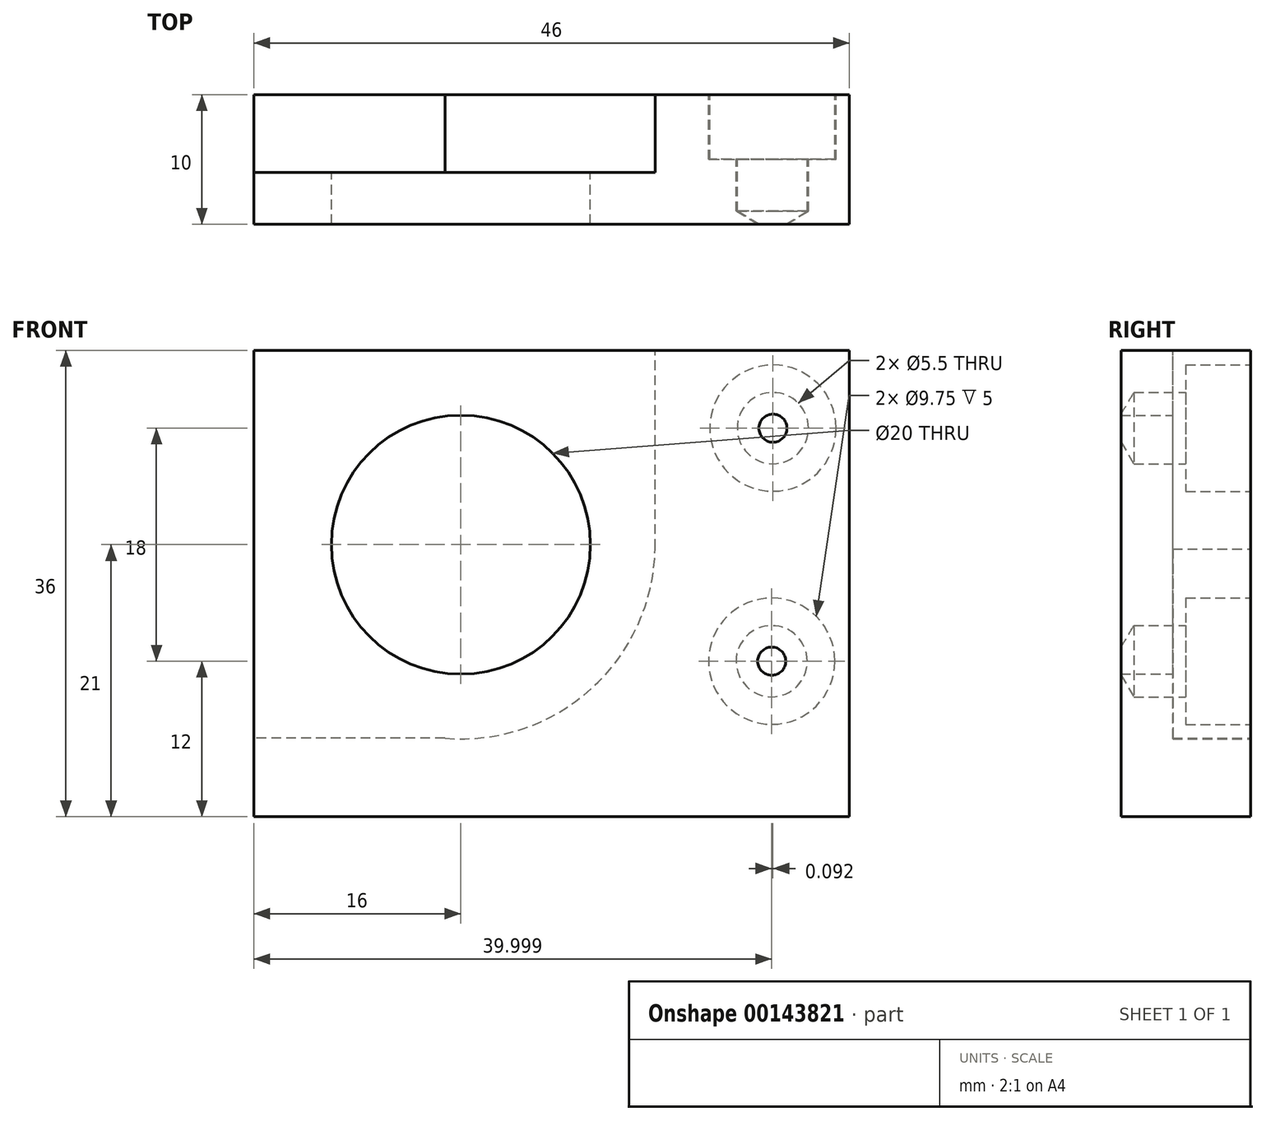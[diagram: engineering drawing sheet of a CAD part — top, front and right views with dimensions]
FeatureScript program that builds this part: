
annotation { "Feature Type Name" : "Feature", "Feature Type Description" : "" }
export const myFeature = defineFeature(function(context is Context, id is Id, definition is map)
    precondition{}
    {
        {
            var Q0;
            Q0=qCreatedBy(makeId("Front.planeOp"),FACE);
            var sketch = newSketch(context, id + "F0", { "sketchPlane" : qUnion([Q0])});
            skLineSegment(sketch, "E0.bottom", {"start": v(23, -18) * mm, "end": v(-23, -18) * mm});
            skLineSegment(sketch, "E0.top", {"start": v(23, 18) * mm, "end": v(-23, 18) * mm});
            skLineSegment(sketch, "E0.left", {"start": v(23, -18) * mm, "end": v(23, 18) * mm});
            skLineSegment(sketch, "E0.right", {"start": v(-23, -18) * mm, "end": v(-23, 18) * mm});
            skPoint(sketch, "E0.middle", {"position": v(0, 0) * mm});
            skCircle(sketch, "E1", {"center": v(-7, 3) * mm, "radius": 10 * mm});
            skSolve(sketch);
        }
        {
            var Q0;
            Q0=makeQuery(id+"F0.imprint","IMPRINT",FACE,{"disambiguationData":[TD([[makeQuery(id+"F0.imprint","IMPRINT",EDGE,{"derivedFrom":sQuery(id+"F0.wireOp",EDGE,"E0.bottom")}),-1.0]])]});
            extrude(context, id + "F1", {"entities" : qUnion([Q0]), "depth" : 10 * mm});
        }
        {
            var Q0;
            Q0=makeQuery(id+"F1.opExtrude","CAP_FACE",FACE,{"disambiguationData":[OSD([sQuery(id+"F0.wireOp",EDGE,"E0.bottom"),sQuery(id+"F0.wireOp",EDGE,"E0.top"),sQuery(id+"F0.wireOp",EDGE,"E0.left"),sQuery(id+"F0.wireOp",EDGE,"E0.right"),sQuery(id+"F0.wireOp",EDGE,"aKu84cq8-YSLd-acEW-WYgU-Aiw9NU1RKzbg")])],"isStart":true});
            var sketch = newSketch(context, id + "F2", { "sketchPlane" : qUnion([Q0])});
            skCircle(sketch, "E2", {"center": v(-17.1, 12) * mm, "radius": 2.46 * mm});
            skCircle(sketch, "E3", {"center": v(-17, -6) * mm, "radius": 2.49 * mm});
            skSolve(sketch);
        }
        {
            var Q0;
            Q0=sQuery(id+"F2.wireOp",VERTEX,"E2.center");
            var Q1;
            Q1=sQuery(id+"F2.wireOp",VERTEX,"E3.center");
            var Q2;
            Q2=makeQuery(id+"F1.opExtrude","SWEPT_BODY",BODY,{"disambiguationData":[OSD([sQuery(id+"F0.wireOp",EDGE,"E0.bottom"),sQuery(id+"F0.wireOp",EDGE,"E0.top"),sQuery(id+"F0.wireOp",EDGE,"E0.left"),sQuery(id+"F0.wireOp",EDGE,"E0.right"),sQuery(id+"F0.wireOp",EDGE,"aKu84cq8-YSLd-acEW-WYgU-Aiw9NU1RKzbg")])]});
            hole(context, id + "F3", {"style" : HoleStyle.C_BORE, "endStyle" : HoleEndStyle.BLIND, "standardTappedOrClearance" : lookupTablePath({ "standard" : "ISO", "fit" : "Normal", "size" : "M5", "type" : "Clearance" }), "standardBlindInLast" : lookupTablePath({ "fit" : "Standard", "standard" : "ISO", "size" : "M5", "type" : "Clearance" }), "holeDiameter" : 5.5 * mm, "cBoreDiameter" : 9.75 * mm, "cBoreDepth" : 5 * mm, "holeDepth" : 9 * mm, "startFromSketch" : true, "locations" : qUnion([Q0, Q1]), "scope" : qUnion([Q2])});
        }
        {
            var Q0;
            Q0=makeQuery(id+"F1.opExtrude","CAP_FACE",FACE,{"disambiguationData":[OSD([sQuery(id+"F0.wireOp",EDGE,"E0.bottom"),sQuery(id+"F0.wireOp",EDGE,"E0.top"),sQuery(id+"F0.wireOp",EDGE,"E0.left"),sQuery(id+"F0.wireOp",EDGE,"E0.right"),sQuery(id+"F0.wireOp",EDGE,"E1")])],"isStart":true});
            var sketch = newSketch(context, id + "F4", { "sketchPlane" : qUnion([Q0])});
            skArc(sketch, "E4", {"start": v(-8, 3.32) * mm, "mid": v(-3.28, -7.92) * mm, "end": v(8.23, -11.95) * mm});
            skLineSegment(sketch, "E5", {"start": v(-8, 2.68) * mm, "end": v(-8, 18) * mm});
            skLineSegment(sketch, "E6", {"start": v(8.23, -11.95) * mm, "end": v(23, -11.95) * mm});
            skSolve(sketch);
        }
        {
            var Q0;
            {var subQ6=sQuery(id+"F4.wireOp",EDGE,"E6");Q0=makeQuery(id+"F4.imprint","IMPRINT",FACE,{"disambiguationData":[TD([[makeQuery(id+"F4.imprint","IMPRINT",EDGE,{"derivedFrom":subQ6}),1.0]])]});}
            extrude(context, id + "F5", {"entities" : qUnion([Q0]), "operationType" : NewBodyOperationType.REMOVE, "oppositeDirection" : true, "depth" : 6 * mm});
        }
    });
